# Revit family: Reece_Laundry Trough_Posh_Domaine_Inset or undermount_45 ltr
name_source: partatom
category: Plumbing Fixtures
revit_build: Autodesk Revit 2018 (Build: 20190510_1515(x64)
units: mm (PartAtom-declared; Revit-internal decimal feet)

## family parameters
Cut with Voids When Loaded = No
Host = Face
Part Type = Normal
Room Calculation Point = Yes
Round Connector Dimension = Use Diameter
Shared = Yes

## types (1)
- 2 Taphole_with Bypass_Stainless Steel
    CWFU = 0
    Default Elevation = 0 mm  [stored 0 ft]
    Description = Posh Domaine Trough 45L with Bypass 2 Taphole Stainless Steel
    Disclaimer = THIS FILE IS THE PROPERTY OF THE REECE GROUP. IT MAY NOT BE REPRODUCED, REVERSE-ENGINEERED OR MODIFIED. ANY REPUBLICATION, TRANSMISSION OR DISTRIBUTION FOR THE PURPOSE OF COMMERCIALLY EXPLOITING THE FILES IS PROHIBITED.
    HWFU = 0
    Keynote = Product #2408001, Reece_Laundry Trough_Posh_Domaine_Inset or undermount_45 ltr - 2 Taphole_with Bypass_Stainless Steel
    Manufacturer = Posh
    Model = Domaine
    Reece_Detail_Additional = With Bypass
    Reece_Detail_Connector = 2 Tapholes
    Reece_Detail_Disclaimer = THIS FILE IS THE PROPERTY OF THE REECE GROUP. IT MAY NOT BE REPRODUCED, REVERSE-ENGINEERED OR MODIFIED. ANY REPUBLICATION, TRANSMISSION OR DISTRIBUTION FOR THE PURPOSE OF COMMERCIALLY EXPLOITING THE FILES IS PROHIBITED.
    Reece_Detail_Installation = Inset/Undermount
    Reece_Material-Main = Reece_Metal_Steel
    Reece_Material_Secondary = Reece_Metal_Steel
    Reece_Overall_Capacity = 45 L
    Reece_Overall_Height = 225 mm  [stored 0.738189 ft]
    Reece_Overall_Length = 500 mm  [stored 1.64042 ft]
    Reece_Overall_Width = 600 mm
    Reece_Product_Brand = Posh
    Reece_Product_Description = Posh Domaine Trough 45L with Bypass 2 Taphole Stainless Steel
    Reece_Product_Mount = Inset / Undermount
    Reece_Product_Number = 2408001
    Reece_Product_Sub Brand = Domaine
    Reece_Product_Type = Laundry Trough
    Reece_Product_Web Page = https://www.reece.com.au
    Reece_Sink_Outlet = 40 mm  [stored 0.131234 ft]
    Reece_Sink_Type = Reece_Laundry Trough_Posh_Domaine_Inset or undermount_45 ltr_Nested : 2 Taphole_with Bypass_Stainless Steel
    Type Comments = Laundry Trough
    URL = https://www.reece.com.au
    WFU = 0

note: [stored X ft] marks values corroborated as IEEE doubles in the binary element streams (Revit-internal decimal feet)

## geometry (parser evidence)
native form markers: Sweep x5
no freeform markers — native parametric forms only
